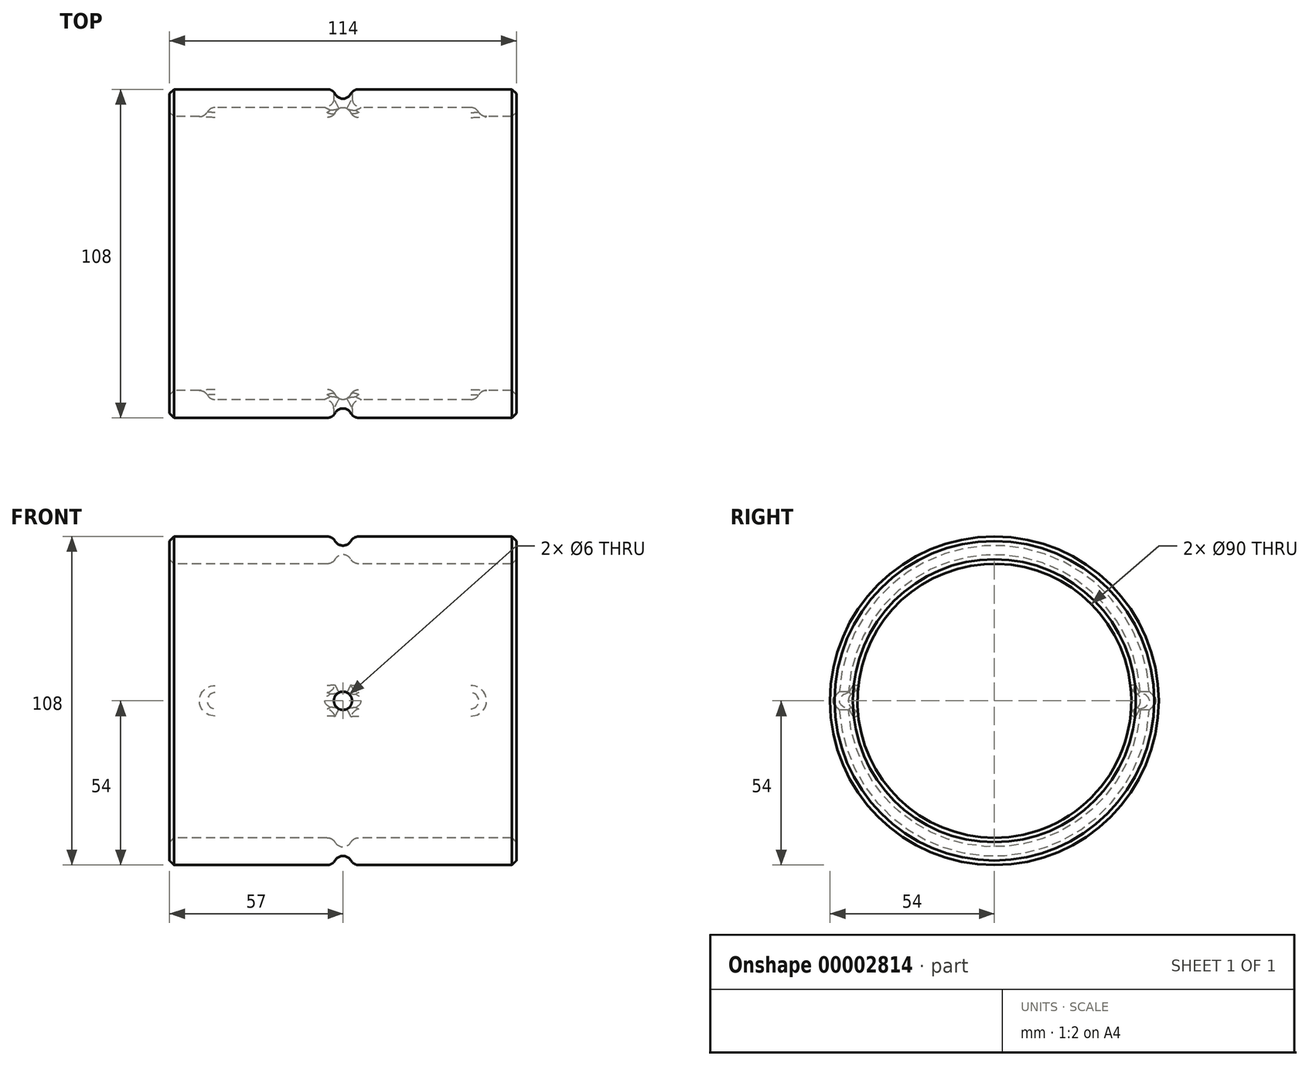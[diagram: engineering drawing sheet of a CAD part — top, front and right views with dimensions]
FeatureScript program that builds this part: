
annotation { "Feature Type Name" : "Feature", "Feature Type Description" : "" }
export const myFeature = defineFeature(function(context is Context, id is Id, definition is map)
    precondition{}
    {
        {
            var Q0;
            Q0=qCreatedBy(makeId("Right.planeOp"),FACE);
            var sketch = newSketch(context, id + "F0", { "sketchPlane" : qUnion([Q0])});
            skCircle(sketch, "E0", {"center": v(0, 0) * mm, "radius": 54 * mm});
            skCircle(sketch, "E1", {"center": v(0, 0) * mm, "radius": 45 * mm});
            skSolve(sketch);
        }
        {
            var Q0;
            Q0 = qSketchRegion(id + "F0", true);
            extrude(context, id + "F1", {"entities" : qUnion([Q0]), "endBound" : BoundingType.SYMMETRIC, "depth" : 114 * mm});
        }
        {
            var Q0;
            Q0=makeQuery(id+"F1.opExtrude","CAP_FACE",FACE,{"disambiguationData":[OSD([sQuery(id+"F0.wireOp",EDGE,"E0"),sQuery(id+"F0.wireOp",EDGE,"E1")])],"isStart":false});
            var Q1;
            Q1=makeQuery(id+"F1.opExtrude","CAP_FACE",FACE,{"disambiguationData":[OSD([sQuery(id+"F0.wireOp",EDGE,"E0"),sQuery(id+"F0.wireOp",EDGE,"E1")])],"isStart":true});
            chamfer(context, id + "F2", {"entities" : qUnion([Q0, Q1]), "width" : 1.5 * mm, "tangentPropagation" : true});
        }
        {
            var Q0;
            Q0=qCreatedBy(makeId("Top.planeOp"),FACE);
            var sketch = newSketch(context, id + "F3", { "sketchPlane" : qUnion([Q0])});
            skLineSegment(sketch, "E2", {"start": v(0, 0) * mm, "end": v(0, 59.06) * mm, "construction": true});
            skLineSegment(sketch, "E3", {"start": v(0, 0) * mm, "end": v(33.45, 0) * mm, "construction": true});
            skLineSegment(sketch, "E4.0", {"start": v(0, 54) * mm, "end": v(33.45, 54) * mm, "construction": true});
            skCircle(sketch, "E5", {"center": v(0, 54) * mm, "radius": 3 * mm});
            skLineSegment(sketch, "E6.0", {"start": v(0, 45) * mm, "end": v(33.45, 45) * mm, "construction": true});
            skCircle(sketch, "E7", {"center": v(0, 45) * mm, "radius": 3 * mm});
            skSolve(sketch);
        }
        {
            var Q0;
            Q0=makeQuery(id+"F3.imprint","IMPRINT",FACE,{"disambiguationData":[TD([[makeQuery(id+"F3.imprint","IMPRINT",EDGE,{"derivedFrom":sQuery(id+"F3.wireOp",EDGE,"E5")}),1.0]])]});
            var Q1;
            Q1=sQuery(id+"F3.wireOp",EDGE,"E3");
            revolve(context, id + "F4", {"entities" : qUnion([Q0]), "axis" : qUnion([Q1]), "revolveType" : RevolveType.FULL});
        }
        {
            var Q0;
            Q0=makeQuery(id+"F3.imprint","IMPRINT",FACE,{"disambiguationData":[TD([[makeQuery(id+"F3.imprint","IMPRINT",EDGE,{"derivedFrom":sQuery(id+"F3.wireOp",EDGE,"E7")}),1.0]])]});
            var Q1;
            Q1=sQuery(id+"F3.wireOp",EDGE,"E3");
            revolve(context, id + "F5", {"entities" : qUnion([Q0]), "axis" : qUnion([Q1]), "revolveType" : RevolveType.FULL});
        }
        {
            var Q0;
            Q0=makeQuery(id+"F4.opRevolve","SWEPT_BODY",BODY,{"disambiguationData":[OSD([sQuery(id+"F3.wireOp",EDGE,"E5")])]});
            var Q1;
            Q1=makeQuery(id+"F5.opRevolve","SWEPT_BODY",BODY,{"disambiguationData":[OSD([sQuery(id+"F3.wireOp",EDGE,"E7")])]});
            var Q2;
            Q2=makeQuery(id+"F1.opExtrude","SWEPT_BODY",BODY,{"disambiguationData":[OSD([sQuery(id+"F0.wireOp",EDGE,"E0"),sQuery(id+"F0.wireOp",EDGE,"E1")])]});
            booleanBodies(context, id + "F6", {"operationType" : BooleanOperationType.SUBTRACTION, "tools" : qUnion([Q0, Q1]), "targets" : qUnion([Q2])});
        }
        {
            var Q0;
            Q0=makeQuery(id+"F6.opBoolean","INTERSECT",EDGE,{"disambiguationData":[OD(1.0)],"derivedFrom":[makeQuery(id+"F1.opExtrude","SWEPT_FACE",FACE,{"disambiguationData":[OSD([sQuery(id+"F0.wireOp",EDGE,"E0")])]}),makeQuery(id+"F4.opRevolve","SWEPT_FACE",FACE,{"disambiguationData":[OSD([sQuery(id+"F3.wireOp",EDGE,"E5")])]})]});
            var Q1;
            Q1=makeQuery(id+"F6.opBoolean","INTERSECT",EDGE,{"disambiguationData":[OD(0.0)],"derivedFrom":[makeQuery(id+"F1.opExtrude","SWEPT_FACE",FACE,{"disambiguationData":[OSD([sQuery(id+"F0.wireOp",EDGE,"E0")])]}),makeQuery(id+"F4.opRevolve","SWEPT_FACE",FACE,{"disambiguationData":[OSD([sQuery(id+"F3.wireOp",EDGE,"E5")])]})]});
            fillet(context, id + "F7", {"entities" : qUnion([Q0, Q1]), "radius" : 3 * mm, "tangentPropagation" : true, "allowEdgeOverflow" : false});
        }
        {
            var Q0;
            Q0=makeQuery(id+"F6.opBoolean","INTERSECT",EDGE,{"disambiguationData":[OD(1.0)],"derivedFrom":[makeQuery(id+"F1.opExtrude","SWEPT_FACE",FACE,{"disambiguationData":[OSD([sQuery(id+"F0.wireOp",EDGE,"E1")])]}),makeQuery(id+"F5.opRevolve","SWEPT_FACE",FACE,{"disambiguationData":[OSD([sQuery(id+"F3.wireOp",EDGE,"E7")])]})]});
            var Q1;
            Q1=makeQuery(id+"F6.opBoolean","INTERSECT",EDGE,{"disambiguationData":[OD(0.0)],"derivedFrom":[makeQuery(id+"F1.opExtrude","SWEPT_FACE",FACE,{"disambiguationData":[OSD([sQuery(id+"F0.wireOp",EDGE,"E1")])]}),makeQuery(id+"F5.opRevolve","SWEPT_FACE",FACE,{"disambiguationData":[OSD([sQuery(id+"F3.wireOp",EDGE,"E7")])]})]});
            fillet(context, id + "F8", {"entities" : qUnion([Q0, Q1]), "radius" : 3 * mm, "tangentPropagation" : true, "allowEdgeOverflow" : false});
        }
        {
            var Q0;
            Q0=qCreatedBy(makeId("Front.planeOp"),FACE);
            var sketch = newSketch(context, id + "F9", { "sketchPlane" : qUnion([Q0])});
            skCircle(sketch, "E8", {"center": v(0, 0) * mm, "radius": 3 * mm});
            skSolve(sketch);
        }
        {
            var Q0;
            Q0 = qSketchRegion(id + "F9", true);
            extrude(context, id + "F10", {"entities" : qUnion([Q0]), "operationType" : NewBodyOperationType.REMOVE, "endBound" : BoundingType.SYMMETRIC, "oppositeDirection" : true, "depth" : 200 * mm});
        }
        {
            var Q0;
            Q0=qCreatedBy(makeId("Right.planeOp"),FACE);
            var sketch = newSketch(context, id + "F11", { "sketchPlane" : qUnion([Q0])});
            skCircle(sketch, "E9.0", {"center": v(0, 0) * mm, "radius": 45 * mm, "construction": true});
            skLineSegment(sketch, "E10", {"start": v(0, 0) * mm, "end": v(45, 0) * mm, "construction": true});
            skCircle(sketch, "E11", {"center": v(45, 0) * mm, "radius": 3 * mm});
            skCircle(sketch, "E12.0.MirrorC", {"center": v(-45, 0) * mm, "radius": 3 * mm});
            skSolve(sketch);
        }
        {
            var Q0;
            Q0 = qSketchRegion(id + "F11", true);
            extrude(context, id + "F12", {"entities" : qUnion([Q0]), "endBound" : BoundingType.SYMMETRIC, "depth" : 90 * mm});
        }
        {
            var Q0;
            Q0=makeQuery(id+"F12.opExtrude","CAP_EDGE",EDGE,{"disambiguationData":[OSD([sQuery(id+"F11.wireOp",EDGE,"E11")])],"isStart":true});
            var Q1;
            Q1=makeQuery(id+"F12.opExtrude","SWEPT_FACE",FACE,{"disambiguationData":[OSD([sQuery(id+"F11.wireOp",EDGE,"E11")])]});
            var Q2;
            Q2=makeQuery(id+"F12.opExtrude","SWEPT_FACE",FACE,{"disambiguationData":[OSD([sQuery(id+"F11.wireOp",EDGE,"E12.0.MirrorC")])]});
            fillet(context, id + "F13", {"entities" : qUnion([Q0, Q1, Q2]), "radius" : 3 * mm, "tangentPropagation" : true, "allowEdgeOverflow" : false});
        }
        {
            var Q0;
            Q0=makeQuery(id+"F12.opExtrude","SWEPT_BODY",BODY,{"disambiguationData":[OSD([sQuery(id+"F11.wireOp",EDGE,"E12.0.MirrorC")])]});
            var Q1;
            Q1=makeQuery(id+"F12.opExtrude","SWEPT_BODY",BODY,{"disambiguationData":[OSD([sQuery(id+"F11.wireOp",EDGE,"E11")])]});
            var Q2;
            Q2=makeQuery(id+"F1.opExtrude","SWEPT_BODY",BODY,{"disambiguationData":[OSD([sQuery(id+"F0.wireOp",EDGE,"E0"),sQuery(id+"F0.wireOp",EDGE,"E1")])]});
            booleanBodies(context, id + "F14", {"operationType" : BooleanOperationType.SUBTRACTION, "tools" : qUnion([Q0, Q1]), "targets" : qUnion([Q2])});
        }
        {
            var Q0;
            Q0=makeQuery(id+"F14.opBoolean","COPY",FACE,{"disambiguationData":[OD(0.0)],"derivedFrom":makeQuery(id+"F12.opExtrude","SWEPT_FACE",FACE,{"disambiguationData":[OSD([sQuery(id+"F11.wireOp",EDGE,"E11")])]})});
            var Q1;
            Q1=makeQuery(id+"F14.opBoolean","COPY",FACE,{"disambiguationData":[OD(1.0)],"derivedFrom":makeQuery(id+"F12.opExtrude","SWEPT_FACE",FACE,{"disambiguationData":[OSD([sQuery(id+"F11.wireOp",EDGE,"E11")])]})});
            var Q2;
            Q2=makeQuery(id+"F14.opBoolean","COPY",FACE,{"disambiguationData":[OD(1.0)],"derivedFrom":makeQuery(id+"F12.opExtrude","SWEPT_FACE",FACE,{"disambiguationData":[OSD([sQuery(id+"F11.wireOp",EDGE,"E12.0.MirrorC")])]})});
            var Q3;
            Q3=makeQuery(id+"F14.opBoolean","COPY",FACE,{"disambiguationData":[OD(0.0)],"derivedFrom":makeQuery(id+"F12.opExtrude","SWEPT_FACE",FACE,{"disambiguationData":[OSD([sQuery(id+"F11.wireOp",EDGE,"E12.0.MirrorC")])]})});
            fillet(context, id + "F15", {"entities" : qUnion([Q0, Q1, Q2, Q3]), "radius" : 3 * mm, "tangentPropagation" : true, "allowEdgeOverflow" : false});
        }
    });
